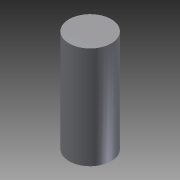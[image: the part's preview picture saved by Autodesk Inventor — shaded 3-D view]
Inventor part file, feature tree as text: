
AUTODESK INVENTOR PART (.ipt)
format: ipt  version: 2011 (Build 150230000, 230)  size: 83,456 bytes
history: native  units: mm
features: extrude x1, sketch x1
ambient origin geometry x8: Origin, YZ Plane, XZ Plane, XY Plane, X Axis, Y Axis, Z Axis, Center Point
bodies: Solid1 (feature_tree)
feature tree (2):
  extrude  "Extrusion1"  TaperAngle=0.0deg  [1 undecoded]
  sketch  "Sketch1"  dims[d2=0.0mm d3=0.0mm d4=0.0mm d9=0.0mm d10=0.0mm]
note: 1 required parameter value undecoded (feature->parameter linkage not recoverable at this tier; creation-order binding heuristic only, values carry confidence <= 0.55)
